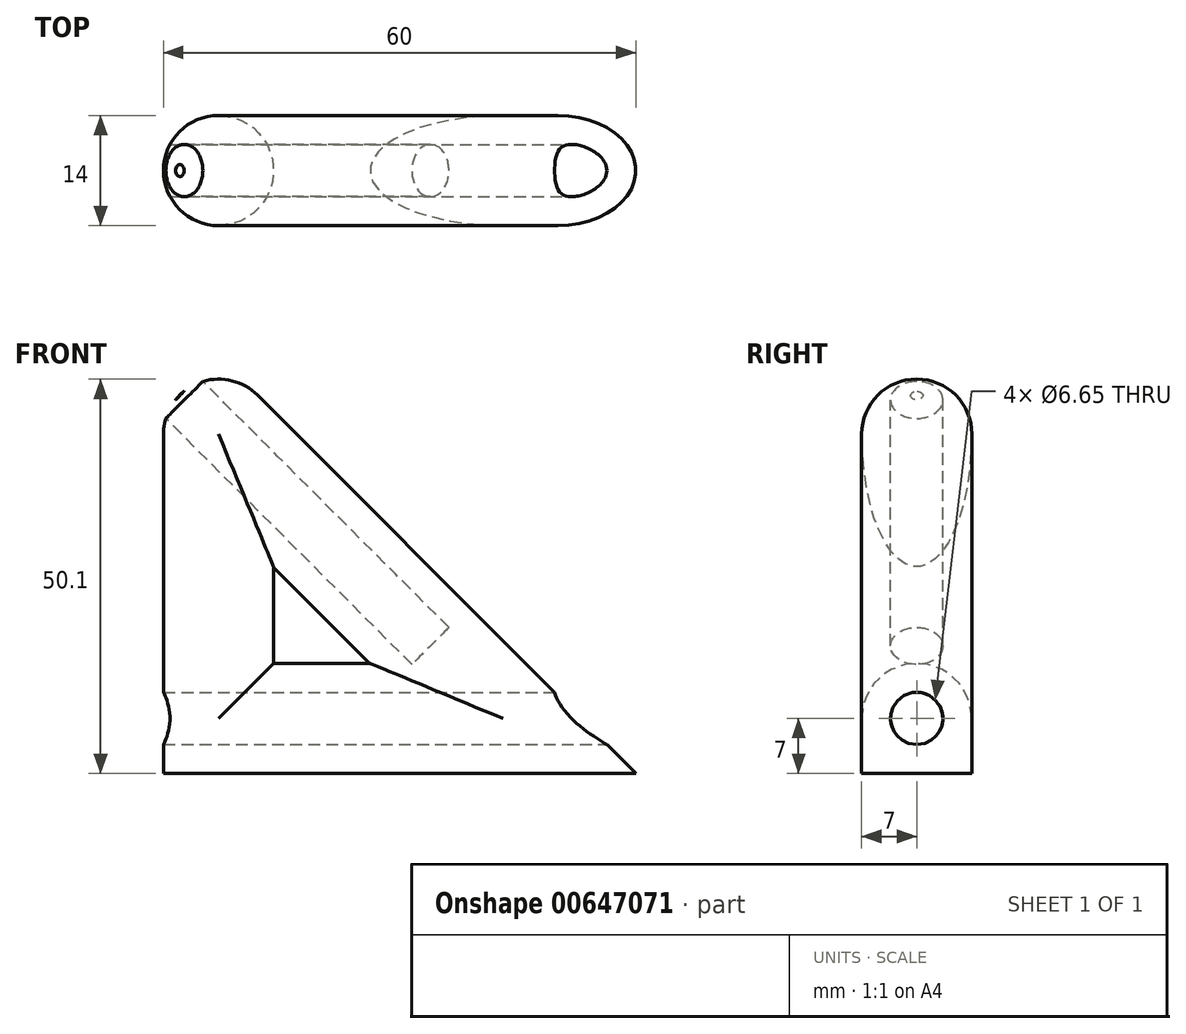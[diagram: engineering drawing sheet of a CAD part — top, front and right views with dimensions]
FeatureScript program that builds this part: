
annotation { "Feature Type Name" : "Feature", "Feature Type Description" : "" }
export const myFeature = defineFeature(function(context is Context, id is Id, definition is map)
    precondition{}
    {
        {
            var Q0;
            Q0=qCreatedBy(makeId("Front.planeOp"),FACE);
            var sketch = newSketch(context, id + "F0", { "sketchPlane" : qUnion([Q0])});
            skLineSegment(sketch, "E0", {"start": v(0, 0) * mm, "end": v(-48.05, 48.05) * mm});
            skLineSegment(sketch, "E1", {"start": v(-60, 43.1) * mm, "end": v(-60, 0) * mm});
            skLineSegment(sketch, "E2", {"start": v(-60, 0) * mm, "end": v(0, 0) * mm});
            skLineSegment(sketch, "E3", {"start": v(-64.77, 54.93) * mm, "end": v(-4.37, -5.47) * mm, "construction": true});
            skLineSegment(sketch, "E4", {"start": v(-65.28, 7) * mm, "end": v(6.98, 7) * mm, "construction": true});
            skPoint(sketch, "E5.visualSharp", {"position": v(-60, 60) * mm});
            skArc(sketch, "E5.filletArc", {"start": v(-48.05, 48.05) * mm, "mid": v(-55.68, 49.57) * mm, "end": v(-60, 43.1) * mm});
            skLineSegment(sketch, "E6.0", {"start": v(-46, 14) * mm, "end": v(-33.8, 14) * mm});
            skLineSegment(sketch, "E7.trimOffspring", {"start": v(-46, 26.2) * mm, "end": v(-46, 14) * mm});
            skLineSegment(sketch, "E8.trimOffspring", {"start": v(-33.8, 14) * mm, "end": v(-46, 26.2) * mm});
            skLineSegment(sketch, "E9", {"start": v(-57.89, 48.05) * mm, "end": v(-50.4, 55.53) * mm});
            skSolve(sketch);
        }
        {
            var Q0;
            Q0=makeQuery(id+"F0.imprint","IMPRINT",FACE,{"disambiguationData":[TD([[makeQuery(id+"F0.imprint","IMPRINT",EDGE,{"derivedFrom":sQuery(id+"F0.wireOp",EDGE,"E0")}),1.0]])]});
            extrude(context, id + "F1", {"entities" : qUnion([Q0]), "depth" : 14 * mm, "offsetDistance" : 25 * mm});
        }
        {
            var Q0;
            Q0=makeQuery(id+"F1.opExtrude","CAP_EDGE",EDGE,{"disambiguationData":[OSD([sQuery(id+"F0.wireOp",EDGE,"E0")])],"isStart":false});
            var Q1;
            Q1=makeQuery(id+"F1.opExtrude","CAP_EDGE",EDGE,{"disambiguationData":[OSD([sQuery(id+"F0.wireOp",EDGE,"E8.trimOffspring")])],"isStart":false});
            var Q2;
            Q2=makeQuery(id+"F1.opExtrude","CAP_EDGE",EDGE,{"disambiguationData":[OSD([sQuery(id+"F0.wireOp",EDGE,"E7.trimOffspring")])],"isStart":false});
            var Q3;
            Q3=makeQuery(id+"F1.opExtrude","CAP_EDGE",EDGE,{"disambiguationData":[OSD([sQuery(id+"F0.wireOp",EDGE,"E6.0")])],"isStart":false});
            var Q4;
            Q4=makeQuery(id+"F1.opExtrude","CAP_EDGE",EDGE,{"disambiguationData":[OSD([sQuery(id+"F0.wireOp",EDGE,"E0")])],"isStart":true});
            var Q5;
            Q5=makeQuery(id+"F1.opExtrude","CAP_EDGE",EDGE,{"disambiguationData":[OSD([sQuery(id+"F0.wireOp",EDGE,"E8.trimOffspring")])],"isStart":true});
            var Q6;
            Q6=makeQuery(id+"F1.opExtrude","CAP_EDGE",EDGE,{"disambiguationData":[OSD([sQuery(id+"F0.wireOp",EDGE,"E7.trimOffspring")])],"isStart":true});
            var Q7;
            Q7=makeQuery(id+"F1.opExtrude","CAP_EDGE",EDGE,{"disambiguationData":[OSD([sQuery(id+"F0.wireOp",EDGE,"E6.0")])],"isStart":true});
            fillet(context, id + "F2", {"entities" : qUnion([Q0, Q1, Q2, Q3, Q4, Q5, Q6, Q7]), "radius" : 7 * mm, "tangentPropagation" : true, "allowEdgeOverflow" : false});
        }
        {
            var Q0;
            Q0=qCreatedBy(makeId("Right.planeOp"),FACE);
            var sketch = newSketch(context, id + "F3", { "sketchPlane" : qUnion([Q0])});
            skCircle(sketch, "E10", {"center": v(-7, 7) * mm, "radius": 3.33 * mm});
            skSolve(sketch);
        }
        {
            var Q0;
            Q0=makeQuery(id+"F3.imprint","IMPRINT",FACE,{"disambiguationData":[TD([[makeQuery(id+"F3.imprint","IMPRINT",EDGE,{"derivedFrom":sQuery(id+"F3.wireOp",EDGE,"E10")}),1.0]])]});
            extrude(context, id + "F4", {"entities" : qUnion([Q0]), "operationType" : NewBodyOperationType.REMOVE, "oppositeDirection" : true, "depth" : 75 * mm, "offsetDistance" : 25 * mm});
        }
        {
            var Q0;
            Q0=sQuery(id+"F0.wireOp",EDGE,"E9");
            cPlane(context, id + "F5", {"entities" : qUnion([Q0]), "cplaneType" : CPlaneType.LINE_ANGLE, "offset" : 25 * mm, "angle" : 90 * degree, "width" : 150 * mm, "height" : 150 * mm});
        }
        {
            var Q0;
            Q0=qCreatedBy(id+"F5.planeOp",FACE);
            var sketch = newSketch(context, id + "F6", { "sketchPlane" : qUnion([Q0])});
            skCircle(sketch, "E11", {"center": v(7, -7) * mm, "radius": 3.33 * mm});
            skSolve(sketch);
        }
        {
            var Q0;
            Q0=makeQuery(id+"F6.imprint","IMPRINT",FACE,{"disambiguationData":[TD([[makeQuery(id+"F6.imprint","IMPRINT",EDGE,{"derivedFrom":sQuery(id+"F6.wireOp",EDGE,"E11")}),1.0]])]});
            extrude(context, id + "F7", {"entities" : qUnion([Q0]), "operationType" : NewBodyOperationType.REMOVE, "oppositeDirection" : true, "depth" : 45 * mm, "offsetDistance" : 25 * mm});
        }
    });
